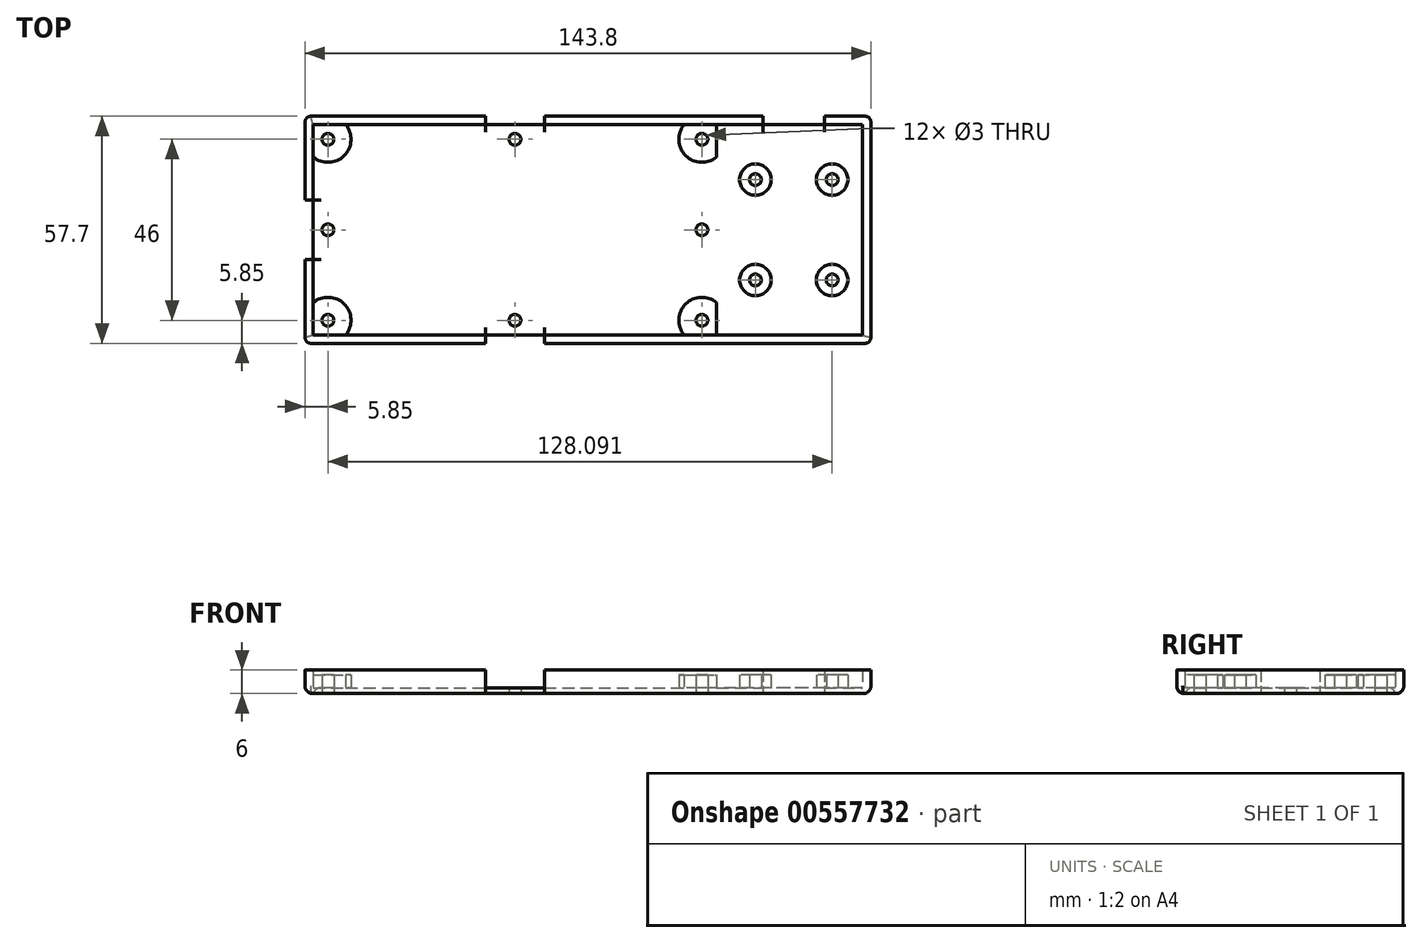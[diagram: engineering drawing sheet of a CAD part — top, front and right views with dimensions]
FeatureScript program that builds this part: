
annotation { "Feature Type Name" : "Feature", "Feature Type Description" : "" }
export const myFeature = defineFeature(function(context is Context, id is Id, definition is map)
    precondition{}
    {
        {
            assignVariable(context, id + "F0", {"name" : "Grosor", "anyValue" : 1.3});
        }
        {
            assignVariable(context, id + "F1", {"name" : "Paredes", "anyValue" : 2.1});
        }
        {
            var Q0;
            Q0=qCreatedBy(makeId("Top.planeOp"),FACE);
            var sketch = newSketch(context, id + "F2", { "sketchPlane" : qUnion([Q0])});
            skLineSegment(sketch, "E0.bottom", {"start": v(-51.25, 26.75) * mm, "end": v(51.25, 26.75) * mm});
            skLineSegment(sketch, "E0.top", {"start": v(-43.01, -26.75) * mm, "end": v(51.25, -26.75) * mm});
            skLineSegment(sketch, "E0.left", {"start": v(-51.25, 26.75) * mm, "end": v(-51.25, -18.51) * mm});
            skLineSegment(sketch, "E0.right", {"start": v(51.25, 26.75) * mm, "end": v(51.25, -26.75) * mm});
            skPoint(sketch, "E0.middle", {"position": v(0, 0) * mm});
            skLineSegment(sketch, "E1.0", {"start": v(-53.35, -28.85) * mm, "end": v(53.35, -28.85) * mm});
            skLineSegment(sketch, "E1.1", {"start": v(-53.35, 28.85) * mm, "end": v(-53.35, -28.85) * mm});
            skLineSegment(sketch, "E1.2", {"start": v(-53.35, 28.85) * mm, "end": v(53.35, 28.85) * mm});
            skLineSegment(sketch, "E1.3", {"start": v(53.35, 28.85) * mm, "end": v(53.35, -28.85) * mm});
            skLineSegment(sketch, "E2.bottom", {"start": v(-47.5, 23) * mm, "end": v(47.5, 23) * mm, "construction": true});
            skLineSegment(sketch, "E2.top", {"start": v(-47.5, -23) * mm, "end": v(47.5, -23) * mm, "construction": true});
            skLineSegment(sketch, "E2.left", {"start": v(-47.5, 23) * mm, "end": v(-47.5, -23) * mm, "construction": true});
            skLineSegment(sketch, "E2.right", {"start": v(47.5, 23) * mm, "end": v(47.5, -23) * mm, "construction": true});
            skCircle(sketch, "E3", {"center": v(47.5, 23) * mm, "radius": 1.5 * mm});
            skCircle(sketch, "E4", {"center": v(47.5, -23) * mm, "radius": 1.5 * mm});
            skCircle(sketch, "E5", {"center": v(-47.5, -23) * mm, "radius": 1.5 * mm});
            skCircle(sketch, "E6", {"center": v(-47.5, 23) * mm, "radius": 1.5 * mm});
            skArc(sketch, "E7", {"start": v(-51.25, 18.51) * mm, "mid": v(-43.36, 18.86) * mm, "end": v(-43.01, 26.75) * mm});
            skArc(sketch, "E8", {"start": v(43.01, 26.75) * mm, "mid": v(43.36, 18.86) * mm, "end": v(51.25, 18.51) * mm});
            skArc(sketch, "E9", {"start": v(51.25, -18.51) * mm, "mid": v(43.36, -18.86) * mm, "end": v(43.01, -26.75) * mm});
            skArc(sketch, "E10.trimOffspring", {"start": v(-43.01, -26.75) * mm, "mid": v(-43.36, -18.86) * mm, "end": v(-51.25, -18.51) * mm});
            skPoint(sketch, "E11.orphan", {"position": v(-51.25, -26.75) * mm});
            skLineSegment(sketch, "E12", {"start": v(-51.25, -18.51) * mm, "end": v(-51.25, -26.75) * mm});
            skLineSegment(sketch, "E13", {"start": v(-43.01, -26.75) * mm, "end": v(-51.25, -26.75) * mm});
            skLineSegment(sketch, "E14.bottom", {"start": v(53.35, -7.5) * mm, "end": v(-53.35, -7.5) * mm});
            skLineSegment(sketch, "E14.top", {"start": v(53.35, 7.5) * mm, "end": v(-53.35, 7.5) * mm});
            skLineSegment(sketch, "E14.left", {"start": v(53.35, -7.5) * mm, "end": v(53.35, 7.5) * mm});
            skLineSegment(sketch, "E14.right", {"start": v(-53.35, -7.5) * mm, "end": v(-53.35, 7.5) * mm});
            skLineSegment(sketch, "E15.bottom", {"start": v(-7.5, 28.85) * mm, "end": v(7.5, 28.85) * mm});
            skLineSegment(sketch, "E15.top", {"start": v(-7.5, -28.85) * mm, "end": v(7.5, -28.85) * mm});
            skLineSegment(sketch, "E15.left", {"start": v(-7.5, 28.85) * mm, "end": v(-7.5, -28.85) * mm});
            skLineSegment(sketch, "E15.right", {"start": v(7.5, 28.85) * mm, "end": v(7.5, -28.85) * mm});
            skCircle(sketch, "E16", {"center": v(-47.5, 0) * mm, "radius": 1.5 * mm});
            skCircle(sketch, "E17", {"center": v(0, 23) * mm, "radius": 1.5 * mm});
            skCircle(sketch, "E18", {"center": v(0, -23) * mm, "radius": 1.5 * mm});
            skCircle(sketch, "E19", {"center": v(47.5, 0) * mm, "radius": 1.5 * mm});
            skLineSegment(sketch, "E20", {"start": v(53.35, 28.85) * mm, "end": v(90.45, 28.85) * mm});
            skLineSegment(sketch, "E21", {"start": v(90.45, 28.85) * mm, "end": v(90.45, -28.85) * mm});
            skLineSegment(sketch, "E22", {"start": v(90.45, -28.85) * mm, "end": v(53.35, -28.85) * mm});
            skLineSegment(sketch, "E23.0", {"start": v(88.35, -26.75) * mm, "end": v(53.35, -26.75) * mm});
            skLineSegment(sketch, "E23.1", {"start": v(88.35, 26.75) * mm, "end": v(88.35, -26.75) * mm});
            skLineSegment(sketch, "E23.2", {"start": v(53.33, 26.75) * mm, "end": v(88.35, 26.75) * mm});
            skLineSegment(sketch, "E24", {"start": v(70.84, 26.75) * mm, "end": v(70.84, 0) * mm, "construction": true});
            skPoint(sketch, "E24.endSnap0", {"position": v(88.35, 0) * mm});
            skLineSegment(sketch, "E25.bottom", {"start": v(80.6, -12.75) * mm, "end": v(61.1, -12.75) * mm, "construction": true});
            skLineSegment(sketch, "E25.top", {"start": v(80.6, 12.75) * mm, "end": v(61.1, 12.75) * mm, "construction": true});
            skLineSegment(sketch, "E25.left", {"start": v(80.6, -12.75) * mm, "end": v(80.6, 12.75) * mm, "construction": true});
            skLineSegment(sketch, "E25.right", {"start": v(61.1, -12.75) * mm, "end": v(61.1, 12.75) * mm, "construction": true});
            skPoint(sketch, "E25.middle", {"position": v(70.84, 0) * mm});
            skCircle(sketch, "E26", {"center": v(61.1, 12.75) * mm, "radius": 1.5 * mm});
            skCircle(sketch, "E27", {"center": v(80.6, 12.75) * mm, "radius": 1.5 * mm});
            skCircle(sketch, "E28", {"center": v(80.6, -12.75) * mm, "radius": 1.5 * mm});
            skCircle(sketch, "E29", {"center": v(61.1, -12.75) * mm, "radius": 1.5 * mm});
            skCircle(sketch, "E30", {"center": v(61.1, 12.75) * mm, "radius": 4 * mm});
            skCircle(sketch, "E31", {"center": v(80.6, 12.75) * mm, "radius": 4 * mm});
            skCircle(sketch, "E32", {"center": v(80.6, -12.75) * mm, "radius": 4 * mm});
            skCircle(sketch, "E33", {"center": v(61.1, -12.75) * mm, "radius": 4 * mm});
            skLineSegment(sketch, "E34", {"start": v(51.25, 26.75) * mm, "end": v(51.25, 28.85) * mm});
            skLineSegment(sketch, "E35", {"start": v(51.25, -26.75) * mm, "end": v(51.25, -28.85) * mm});
            skLineSegment(sketch, "E36", {"start": v(51.25, 26.75) * mm, "end": v(53.33, 26.75) * mm});
            skLineSegment(sketch, "E37", {"start": v(51.25, -26.75) * mm, "end": v(53.35, -26.75) * mm});
            skLineSegment(sketch, "E38.bottom", {"start": v(63, 26.75) * mm, "end": v(78.7, 26.75) * mm});
            skLineSegment(sketch, "E38.top", {"start": v(63, 28.85) * mm, "end": v(78.7, 28.85) * mm});
            skLineSegment(sketch, "E38.left", {"start": v(63, 26.75) * mm, "end": v(63, 28.85) * mm});
            skLineSegment(sketch, "E38.right", {"start": v(78.7, 26.75) * mm, "end": v(78.7, 28.85) * mm});
            skPoint(sketch, "E38.middle", {"position": v(70.84, 27.8) * mm});
            skPoint(sketch, "E38.middle.positionSnap0", {"position": v(51.25, 27.8) * mm});
            skPoint(sketch, "E38.centerSnap0", {"position": v(51.25, 27.8) * mm});
            skSolve(sketch);
        }
        {
            var Q0;
            {var subQ5=sQuery(id+"F2.wireOp",EDGE,"E7");Q0=makeQuery(id+"F2.imprint","IMPRINT",FACE,{"disambiguationData":[TD([[makeQuery(id+"F2.imprint","IMPRINT",EDGE,{"derivedFrom":subQ5}),-1.0]])]});}
            var Q1;
            Q1=makeQuery(id+"F2.imprint","IMPRINT",FACE,{"disambiguationData":[TD([[makeQuery(id+"F2.imprint","IMPRINT",EDGE,{"derivedFrom":sQuery(id+"F2.wireOp",EDGE,"E16")}),-1.0]])]});
            var Q2;
            {var subQ7=sQuery(id+"F2.wireOp",EDGE,"E10.trimOffspring");Q2=makeQuery(id+"F2.imprint","IMPRINT",FACE,{"disambiguationData":[TD([[makeQuery(id+"F2.imprint","IMPRINT",EDGE,{"derivedFrom":subQ7}),-1.0]])]});}
            var Q3;
            Q3=makeQuery(id+"F2.imprint","IMPRINT",FACE,{"disambiguationData":[TD([[makeQuery(id+"F2.imprint","IMPRINT",EDGE,{"derivedFrom":sQuery(id+"F2.wireOp",EDGE,"E18")}),-1.0]])]});
            var Q4;
            {var subQ5=sQuery(id+"F2.wireOp",EDGE,"E9");Q4=makeQuery(id+"F2.imprint","IMPRINT",FACE,{"disambiguationData":[TD([[makeQuery(id+"F2.imprint","IMPRINT",EDGE,{"derivedFrom":subQ5}),-1.0]])]});}
            var Q5;
            Q5=makeQuery(id+"F2.imprint","IMPRINT",FACE,{"disambiguationData":[TD([[makeQuery(id+"F2.imprint","IMPRINT",EDGE,{"derivedFrom":sQuery(id+"F2.wireOp",EDGE,"E19")}),-1.0]])]});
            var Q6;
            {var subQ7=sQuery(id+"F2.wireOp",EDGE,"E8");Q6=makeQuery(id+"F2.imprint","IMPRINT",FACE,{"disambiguationData":[TD([[makeQuery(id+"F2.imprint","IMPRINT",EDGE,{"derivedFrom":subQ7}),-1.0]])]});}
            var Q7;
            Q7=makeQuery(id+"F2.imprint","IMPRINT",FACE,{"disambiguationData":[TD([[makeQuery(id+"F2.imprint","IMPRINT",EDGE,{"derivedFrom":sQuery(id+"F2.wireOp",EDGE,"E17")}),-1.0]])]});
            var Q8;
            {var subQ0=sQuery(id+"F2.wireOp",EDGE,"E15.left");var subQ1=sQuery(id+"F2.wireOp",EDGE,"E14.bottom");var subQ2=makeQuery(id+"F2.imprint","INTERSECT",VERTEX,{"derivedFrom":[subQ1,subQ0]});Q8=makeQuery(id+"F2.imprint","IMPRINT",FACE,{"disambiguationData":[TD([[makeQuery(id+"F2.imprint","IMPRINT",EDGE,{"disambiguationData":[TD([[subQ2,1.0]])],"derivedFrom":subQ1}),-1.0]])]});}
            var Q9;
            {var subQ8=sQuery(id+"F2.wireOp",EDGE,"E23.0");Q9=makeQuery(id+"F2.imprint","IMPRINT",FACE,{"disambiguationData":[TD([[makeQuery(id+"F2.imprint","IMPRINT",EDGE,{"derivedFrom":subQ8}),-1.0]])]});}
            var Q10;
            {var subQ8=sQuery(id+"F2.wireOp",EDGE,"E36");Q10=makeQuery(id+"F2.imprint","IMPRINT",FACE,{"disambiguationData":[TD([[makeQuery(id+"F2.imprint","IMPRINT",EDGE,{"derivedFrom":subQ8}),-1.0]])]});}
            var Q11;
            {var subQ0=sQuery(id+"F2.wireOp",EDGE,"E14.top");var subQ1=sQuery(id+"F2.wireOp",EDGE,"E0.right");var subQ2=makeQuery(id+"F2.imprint","INTERSECT",VERTEX,{"derivedFrom":[subQ1,subQ0]});Q11=makeQuery(id+"F2.imprint","IMPRINT",FACE,{"disambiguationData":[TD([[makeQuery(id+"F2.imprint","IMPRINT",EDGE,{"disambiguationData":[TD([[subQ2,-1.0]])],"derivedFrom":subQ1}),1.0]])]});}
            var Q12;
            {var subQ5=sQuery(id+"F2.wireOp",EDGE,"E37");Q12=makeQuery(id+"F2.imprint","IMPRINT",FACE,{"disambiguationData":[TD([[makeQuery(id+"F2.imprint","IMPRINT",EDGE,{"derivedFrom":subQ5}),1.0]])]});}
            extrude(context, id + "F3", {"entities" : qUnion([Q0, Q1, Q2, Q3, Q4, Q5, Q6, Q7, Q8, Q9, Q10, Q11, Q12]), "depth" : (getVariable(context, 'Paredes') - 0.6) * mm, "offsetDistance" : 25 * mm});
        }
        {
            var Q0;
            Q0=makeQuery(id+"F2.imprint","IMPRINT",FACE,{"disambiguationData":[TD([[makeQuery(id+"F2.imprint","IMPRINT",EDGE,{"derivedFrom":sQuery(id+"F2.wireOp",EDGE,"E5")}),-1.0]])]});
            var Q1;
            Q1=makeQuery(id+"F2.imprint","IMPRINT",FACE,{"disambiguationData":[TD([[makeQuery(id+"F2.imprint","IMPRINT",EDGE,{"derivedFrom":sQuery(id+"F2.wireOp",EDGE,"E4")}),-1.0]])]});
            var Q2;
            Q2=makeQuery(id+"F2.imprint","IMPRINT",FACE,{"disambiguationData":[TD([[makeQuery(id+"F2.imprint","IMPRINT",EDGE,{"derivedFrom":sQuery(id+"F2.wireOp",EDGE,"E3")}),-1.0]])]});
            var Q3;
            Q3=makeQuery(id+"F2.imprint","IMPRINT",FACE,{"disambiguationData":[TD([[makeQuery(id+"F2.imprint","IMPRINT",EDGE,{"derivedFrom":sQuery(id+"F2.wireOp",EDGE,"E6")}),-1.0]])]});
            var Q4;
            Q4=makeQuery(id+"F2.imprint","IMPRINT",FACE,{"disambiguationData":[TD([[makeQuery(id+"F2.imprint","IMPRINT",EDGE,{"derivedFrom":sQuery(id+"F2.wireOp",EDGE,"E26")}),-1.0]])]});
            var Q5;
            Q5=makeQuery(id+"F2.imprint","IMPRINT",FACE,{"disambiguationData":[TD([[makeQuery(id+"F2.imprint","IMPRINT",EDGE,{"derivedFrom":sQuery(id+"F2.wireOp",EDGE,"E27")}),-1.0]])]});
            var Q6;
            Q6=makeQuery(id+"F2.imprint","IMPRINT",FACE,{"disambiguationData":[TD([[makeQuery(id+"F2.imprint","IMPRINT",EDGE,{"derivedFrom":sQuery(id+"F2.wireOp",EDGE,"E29")}),-1.0]])]});
            var Q7;
            Q7=makeQuery(id+"F2.imprint","IMPRINT",FACE,{"disambiguationData":[TD([[makeQuery(id+"F2.imprint","IMPRINT",EDGE,{"derivedFrom":sQuery(id+"F2.wireOp",EDGE,"E28")}),-1.0]])]});
            extrude(context, id + "F4", {"entities" : qUnion([Q0, Q1, Q2, Q3, Q4, Q5, Q6, Q7]), "operationType" : NewBodyOperationType.ADD, "depth" : (getVariable(context, 'Paredes') + (getVariable(context, 'Grosor') * 2)) * mm, "offsetDistance" : 25 * mm});
        }
        {
            var Q0;
            {var subQ7=sQuery(id+"F2.wireOp",EDGE,"E12");Q0=makeQuery(id+"F2.imprint","IMPRINT",FACE,{"disambiguationData":[TD([[makeQuery(id+"F2.imprint","IMPRINT",EDGE,{"derivedFrom":subQ7}),-1.0]])]});}
            var Q1;
            {var subQ3=sQuery(id+"F2.wireOp",EDGE,"E35");Q1=makeQuery(id+"F2.imprint","IMPRINT",FACE,{"disambiguationData":[TD([[makeQuery(id+"F2.imprint","IMPRINT",EDGE,{"derivedFrom":subQ3}),-1.0]])]});}
            var Q2;
            {var subQ0=sQuery(id+"F2.wireOp",EDGE,"E7");var subQ3=sQuery(id+"F2.wireOp",EDGE,"E0.bottom");var subQ5=makeQuery(id+"F2.imprint","INTERSECT",VERTEX,{"derivedFrom":[subQ3,subQ0]});Q2=makeQuery(id+"F2.imprint","IMPRINT",FACE,{"disambiguationData":[TD([[makeQuery(id+"F2.imprint","IMPRINT",EDGE,{"disambiguationData":[TD([[subQ5,-1.0]])],"derivedFrom":subQ3}),1.0]])]});}
            var Q3;
            {var subQ5=sQuery(id+"F2.wireOp",EDGE,"E34");Q3=makeQuery(id+"F2.imprint","IMPRINT",FACE,{"disambiguationData":[TD([[makeQuery(id+"F2.imprint","IMPRINT",EDGE,{"derivedFrom":subQ5}),1.0]])]});}
            var Q4;
            {var subQ5=sQuery(id+"F2.wireOp",EDGE,"E38.left");Q4=makeQuery(id+"F2.imprint","IMPRINT",FACE,{"disambiguationData":[TD([[makeQuery(id+"F2.imprint","IMPRINT",EDGE,{"derivedFrom":subQ5}),1.0]])]});}
            var Q5;
            {var subQ0=sQuery(id+"F2.wireOp",EDGE,"E34");Q5=makeQuery(id+"F2.imprint","IMPRINT",FACE,{"disambiguationData":[TD([[makeQuery(id+"F2.imprint","IMPRINT",EDGE,{"derivedFrom":subQ0}),-1.0]])]});}
            var Q6;
            {var subQ3=sQuery(id+"F2.wireOp",EDGE,"E35");Q6=makeQuery(id+"F2.imprint","IMPRINT",FACE,{"disambiguationData":[TD([[makeQuery(id+"F2.imprint","IMPRINT",EDGE,{"derivedFrom":subQ3}),1.0]])]});}
            var Q7;
            {var subQ1=sQuery(id+"F2.wireOp",EDGE,"E21");Q7=makeQuery(id+"F2.imprint","IMPRINT",FACE,{"disambiguationData":[TD([[makeQuery(id+"F2.imprint","IMPRINT",EDGE,{"derivedFrom":subQ1}),-1.0]])]});}
            extrude(context, id + "F5", {"entities" : qUnion([Q0, Q1, Q2, Q3, Q4, Q5, Q6, Q7]), "operationType" : NewBodyOperationType.ADD, "depth" : (getVariable(context, 'Paredes') + (getVariable(context, 'Grosor') * 3)) * mm, "offsetDistance" : 25 * mm});
        }
        {
            var Q0;
            Q0=makeQuery(id+"F5.opExtrude","SWEPT_EDGE",EDGE,{"disambiguationData":[OSD([sQuery(id+"F2.wireOp",EDGE,"E1.0"),sQuery(id+"F2.wireOp",EDGE,"E1.1")])]});
            var Q1;
            Q1=makeQuery(id+"F5.opExtrude","SWEPT_EDGE",EDGE,{"disambiguationData":[OSD([sQuery(id+"F2.wireOp",EDGE,"E1.1"),sQuery(id+"F2.wireOp",EDGE,"E1.2")])]});
            var Q2;
            Q2=makeQuery(id+"F5.opExtrude","SWEPT_EDGE",EDGE,{"disambiguationData":[OSD([sQuery(id+"F2.wireOp",EDGE,"E1.1"),sQuery(id+"F2.wireOp",EDGE,"E1.2")])]});
            var Q3;
            Q3=makeQuery(id+"F5.opExtrude","SWEPT_EDGE",EDGE,{"disambiguationData":[OSD([sQuery(id+"F2.wireOp",EDGE,"E1.0"),sQuery(id+"F2.wireOp",EDGE,"E1.1")])]});
            var Q4;
            Q4=makeQuery(id+"F5.opExtrude","SWEPT_EDGE",EDGE,{"disambiguationData":[OSD([sQuery(id+"F2.wireOp",EDGE,"E21"),sQuery(id+"F2.wireOp",EDGE,"E22")])]});
            var Q5;
            Q5=makeQuery(id+"F5.opExtrude","SWEPT_EDGE",EDGE,{"disambiguationData":[OSD([sQuery(id+"F2.wireOp",EDGE,"E20"),sQuery(id+"F2.wireOp",EDGE,"E21")])]});
            fillet(context, id + "F6", {"entities" : qUnion([Q0, Q1, Q2, Q3, Q4, Q5]), "radius" : 1.5 * mm, "tangentPropagation" : true, "allowEdgeOverflow" : false});
        }
        {
            var Q0;
            {var subQ0=sQuery(id+"F2.wireOp",EDGE,"E0.bottom");Q0=makeQuery(id+"F5.boolean.opBoolean","SPLIT",EDGE,{"disambiguationData":[topologyDisambiguationEdgeConnected([makeQuery(id+"F5.opExtrude","SWEPT_FACE",FACE,{"disambiguationData":[OSD([subQ0])]})])],"derivedFrom":makeQuery(id+"F3.opExtrude","CAP_EDGE",EDGE,{"disambiguationData":[OSD([subQ0])],"isStart":false})});}
            var Q1;
            Q1=makeQuery(id+"F3.opExtrude","CAP_EDGE",EDGE,{"disambiguationData":[OSD([sQuery(id+"F2.wireOp",EDGE,"E7")])],"isStart":false});
            var Q2;
            {var subQ0=sQuery(id+"F2.wireOp",EDGE,"E36");var subQ1=sQuery(id+"F2.wireOp",EDGE,"E23.2");var subQ2=sQuery(id+"F2.wireOp",EDGE,"E0.bottom");Q2=makeQuery(id+"F5.boolean.opBoolean","SPLIT",EDGE,{"disambiguationData":[topologyDisambiguationEdgeConnected([makeQuery(id+"F5.opExtrude","SWEPT_FACE",FACE,{"disambiguationData":[OSD([subQ2,subQ1,subQ0])]})])],"derivedFrom":makeQuery(id+"F3.opExtrude","CAP_EDGE",EDGE,{"disambiguationData":[OSD([subQ2])],"isStart":false})});}
            var Q3;
            {var subQ0=sQuery(id+"F2.wireOp",EDGE,"E36");var subQ1=sQuery(id+"F2.wireOp",EDGE,"E23.2");var subQ2=sQuery(id+"F2.wireOp",EDGE,"E0.bottom");Q3=makeQuery(id+"F5.boolean.opBoolean","SPLIT",EDGE,{"disambiguationData":[topologyDisambiguationEdgeConnected([makeQuery(id+"F5.opExtrude","SWEPT_FACE",FACE,{"disambiguationData":[OSD([subQ2,subQ1,subQ0])]})])],"derivedFrom":makeQuery(id+"F3.opExtrude","CAP_EDGE",EDGE,{"disambiguationData":[OSD([subQ1,subQ0])],"isStart":false})});}
            var Q4;
            Q4=makeQuery(id+"F3.opExtrude","CAP_EDGE",EDGE,{"disambiguationData":[OSD([sQuery(id+"F2.wireOp",EDGE,"E8")])],"isStart":false});
            var Q5;
            Q5=makeQuery(id+"F3.opExtrude","CAP_EDGE",EDGE,{"disambiguationData":[OSD([sQuery(id+"F2.wireOp",EDGE,"E30")])],"isStart":false});
            var Q6;
            Q6=makeQuery(id+"F3.opExtrude","CAP_EDGE",EDGE,{"disambiguationData":[OSD([sQuery(id+"F2.wireOp",EDGE,"E31")])],"isStart":false});
            var Q7;
            Q7=makeQuery(id+"F3.opExtrude","CAP_EDGE",EDGE,{"disambiguationData":[OSD([sQuery(id+"F2.wireOp",EDGE,"E33")])],"isStart":false});
            var Q8;
            Q8=makeQuery(id+"F3.opExtrude","CAP_EDGE",EDGE,{"disambiguationData":[OSD([sQuery(id+"F2.wireOp",EDGE,"E32")])],"isStart":false});
            var Q9;
            {var subQ0=sQuery(id+"F2.wireOp",EDGE,"E36");var subQ1=sQuery(id+"F2.wireOp",EDGE,"E23.2");Q9=makeQuery(id+"F5.boolean.opBoolean","SPLIT",EDGE,{"disambiguationData":[topologyDisambiguationEdgeConnected([makeQuery(id+"F5.opExtrude","SWEPT_FACE",FACE,{"disambiguationData":[OSD([subQ1])]})])],"derivedFrom":makeQuery(id+"F3.opExtrude","CAP_EDGE",EDGE,{"disambiguationData":[OSD([subQ1,subQ0])],"isStart":false})});}
            var Q10;
            Q10=makeQuery(id+"F3.opExtrude","CAP_EDGE",EDGE,{"disambiguationData":[OSD([sQuery(id+"F2.wireOp",EDGE,"E23.1")])],"isStart":false});
            var Q11;
            {var subQ0=sQuery(id+"F2.wireOp",EDGE,"E0.left");Q11=makeQuery(id+"F5.boolean.opBoolean","SPLIT",EDGE,{"disambiguationData":[topologyDisambiguationEdgeConnected([makeQuery(id+"F5.opExtrude","SWEPT_FACE",FACE,{"disambiguationData":[OSD([subQ0])]})])],"derivedFrom":makeQuery(id+"F3.opExtrude","CAP_EDGE",EDGE,{"disambiguationData":[OSD([subQ0])],"isStart":false})});}
            var Q12;
            {var subQ0=sQuery(id+"F2.wireOp",EDGE,"E0.left");Q12=makeQuery(id+"F5.boolean.opBoolean","SPLIT",EDGE,{"disambiguationData":[topologyDisambiguationEdgeConnected([makeQuery(id+"F5.opExtrude","SWEPT_FACE",FACE,{"disambiguationData":[OSD([subQ0,sQuery(id+"F2.wireOp",EDGE,"E12")])]})])],"derivedFrom":makeQuery(id+"F3.opExtrude","CAP_EDGE",EDGE,{"disambiguationData":[OSD([subQ0])],"isStart":false})});}
            var Q13;
            {var subQ0=sQuery(id+"F2.wireOp",EDGE,"E0.top");Q13=makeQuery(id+"F5.boolean.opBoolean","SPLIT",EDGE,{"disambiguationData":[topologyDisambiguationEdgeConnected([makeQuery(id+"F5.opExtrude","SWEPT_FACE",FACE,{"disambiguationData":[OSD([subQ0,sQuery(id+"F2.wireOp",EDGE,"E13")])]})])],"derivedFrom":makeQuery(id+"F3.opExtrude","CAP_EDGE",EDGE,{"disambiguationData":[OSD([subQ0])],"isStart":false})});}
            var Q14;
            Q14=makeQuery(id+"F3.opExtrude","CAP_EDGE",EDGE,{"disambiguationData":[OSD([sQuery(id+"F2.wireOp",EDGE,"E10.trimOffspring")])],"isStart":false});
            var Q15;
            {var subQ0=sQuery(id+"F2.wireOp",EDGE,"E37");var subQ1=sQuery(id+"F2.wireOp",EDGE,"E23.0");var subQ2=sQuery(id+"F2.wireOp",EDGE,"E0.top");Q15=makeQuery(id+"F5.boolean.opBoolean","SPLIT",EDGE,{"disambiguationData":[topologyDisambiguationEdgeConnected([makeQuery(id+"F5.opExtrude","SWEPT_FACE",FACE,{"disambiguationData":[OSD([subQ2,subQ1,subQ0])]})])],"derivedFrom":makeQuery(id+"F3.opExtrude","CAP_EDGE",EDGE,{"disambiguationData":[OSD([subQ2])],"isStart":false})});}
            var Q16;
            Q16=makeQuery(id+"F3.opExtrude","CAP_EDGE",EDGE,{"disambiguationData":[OSD([sQuery(id+"F2.wireOp",EDGE,"E9")])],"isStart":false});
            var Q17;
            {var subQ0=sQuery(id+"F2.wireOp",EDGE,"E0.right");Q17=makeQuery(id+"F3.opExtrude","CAP_EDGE",EDGE,{"disambiguationData":[OSD([subQ0]),TDD([makeQuery(id+"F2.imprint","IMPRINT",EDGE,{"disambiguationData":[TD([[makeQuery(id+"F2.imprint","INTERSECT",VERTEX,{"derivedFrom":[subQ0,sQuery(id+"F2.wireOp",EDGE,"E8")]}),1.0]])],"derivedFrom":subQ0})])],"isStart":false});}
            var Q18;
            {var subQ0=sQuery(id+"F2.wireOp",EDGE,"E0.right");Q18=makeQuery(id+"F3.opExtrude","CAP_EDGE",EDGE,{"disambiguationData":[OSD([subQ0]),TDD([makeQuery(id+"F2.imprint","IMPRINT",EDGE,{"disambiguationData":[TD([[makeQuery(id+"F2.imprint","INTERSECT",VERTEX,{"derivedFrom":[subQ0,sQuery(id+"F2.wireOp",EDGE,"E9")]}),-1.0]])],"derivedFrom":subQ0})])],"isStart":false});}
            var Q19;
            Q19=makeQuery(id+"F3.opExtrude","CAP_EDGE",EDGE,{"disambiguationData":[OSD([sQuery(id+"F2.wireOp",EDGE,"E23.0"),sQuery(id+"F2.wireOp",EDGE,"E37")])],"isStart":false});
            fillet(context, id + "F7", {"entities" : qUnion([Q0, Q1, Q2, Q3, Q4, Q5, Q6, Q7, Q8, Q9, Q10, Q11, Q12, Q13, Q14, Q15, Q16, Q17, Q18, Q19]), "radius" : 2 * mm, "tangentPropagation" : true, "allowEdgeOverflow" : false});
        }
        {
            var Q0;
            Q0=makeQuery(id+"F5.opExtrude","CAP_EDGE",EDGE,{"disambiguationData":[OSD([sQuery(id+"F2.wireOp",EDGE,"E1.0")])],"isStart":true});
            var Q1;
            {var subQ0=sQuery(id+"F2.wireOp",EDGE,"E37");var subQ1=sQuery(id+"F2.wireOp",EDGE,"E23.2");var subQ2=sQuery(id+"F2.wireOp",EDGE,"E23.1");var subQ3=sQuery(id+"F2.wireOp",EDGE,"E23.0");var subQ4=sQuery(id+"F2.wireOp",EDGE,"E20");var subQ5=sQuery(id+"F2.wireOp",EDGE,"E15.right");var subQ6=sQuery(id+"F2.wireOp",EDGE,"E1.0");var subQ7=sQuery(id+"F2.wireOp",EDGE,"E0.top");var subQ8=sQuery(id+"F2.wireOp",EDGE,"E15.left");var subQ9=sQuery(id+"F2.wireOp",EDGE,"E13");var subQ10=sQuery(id+"F2.wireOp",EDGE,"E12");var subQ11=sQuery(id+"F2.wireOp",EDGE,"E1.1");var subQ12=sQuery(id+"F2.wireOp",EDGE,"E0.left");var subQ13=sQuery(id+"F2.wireOp",EDGE,"E1.2");var subQ14=sQuery(id+"F2.wireOp",EDGE,"E0.bottom");var subQ15=sQuery(id+"F2.wireOp",EDGE,"E36");var subQ16=sQuery(id+"F2.wireOp",EDGE,"E33");var subQ17=sQuery(id+"F2.wireOp",EDGE,"E32");var subQ18=sQuery(id+"F2.wireOp",EDGE,"E31");var subQ19=sQuery(id+"F2.wireOp",EDGE,"E30");var subQ20=sQuery(id+"F2.wireOp",EDGE,"E10.trimOffspring");var subQ21=sQuery(id+"F2.wireOp",EDGE,"E9");var subQ22=sQuery(id+"F2.wireOp",EDGE,"E0.right");var subQ23=sQuery(id+"F2.wireOp",EDGE,"E7");var subQ24=sQuery(id+"F2.wireOp",EDGE,"E8");Q1=makeQuery(id+"F6.opFillet","BLEND_EDGE",EDGE,{"blendedFrom":[makeQuery(id+"F5.opExtrude","SWEPT_EDGE",EDGE,{"disambiguationData":[OSD([subQ6,subQ11])]}),makeQuery(id+"F5.boolean.opBoolean","MERGE",FACE,{"derivedFrom":[makeQuery(id+"F4.boolean.opBoolean","MERGE",FACE,{"derivedFrom":[makeQuery(id+"F3.opExtrude","CAP_FACE",FACE,{"disambiguationData":[OSD([subQ14,subQ7,subQ12,subQ22,subQ23,subQ24,subQ21,subQ20,sQuery(id+"F2.wireOp",EDGE,"E16"),sQuery(id+"F2.wireOp",EDGE,"E17"),sQuery(id+"F2.wireOp",EDGE,"E18"),sQuery(id+"F2.wireOp",EDGE,"E19"),subQ3,subQ2,subQ1,subQ19,subQ18,subQ17,subQ16,subQ15,subQ0])],"isStart":true}),makeQuery(id+"F4.opExtrude","CAP_FACE",FACE,{"disambiguationData":[OSD([subQ14,subQ22,sQuery(id+"F2.wireOp",EDGE,"E3"),subQ24])],"isStart":true}),makeQuery(id+"F4.opExtrude","CAP_FACE",FACE,{"disambiguationData":[OSD([subQ14,subQ12,sQuery(id+"F2.wireOp",EDGE,"E6"),subQ23])],"isStart":true}),makeQuery(id+"F4.opExtrude","CAP_FACE",FACE,{"disambiguationData":[OSD([subQ7,subQ22,sQuery(id+"F2.wireOp",EDGE,"E4"),subQ21])],"isStart":true}),makeQuery(id+"F4.opExtrude","CAP_FACE",FACE,{"disambiguationData":[OSD([sQuery(id+"F2.wireOp",EDGE,"E5"),subQ20,subQ10,subQ9])],"isStart":true}),makeQuery(id+"F4.opExtrude","CAP_FACE",FACE,{"disambiguationData":[OSD([sQuery(id+"F2.wireOp",EDGE,"E26"),subQ19])],"isStart":true}),makeQuery(id+"F4.opExtrude","CAP_FACE",FACE,{"disambiguationData":[OSD([sQuery(id+"F2.wireOp",EDGE,"E27"),subQ18])],"isStart":true}),makeQuery(id+"F4.opExtrude","CAP_FACE",FACE,{"disambiguationData":[OSD([sQuery(id+"F2.wireOp",EDGE,"E28"),subQ17])],"isStart":true}),makeQuery(id+"F4.opExtrude","CAP_FACE",FACE,{"disambiguationData":[OSD([sQuery(id+"F2.wireOp",EDGE,"E29"),subQ16])],"isStart":true})]}),makeQuery(id+"F5.opExtrude","CAP_FACE",FACE,{"disambiguationData":[OSD([subQ14,subQ13,subQ5,subQ4,subQ1,subQ15,sQuery(id+"F2.wireOp",EDGE,"E38.left")])],"isStart":true}),makeQuery(id+"F5.opExtrude","CAP_FACE",FACE,{"disambiguationData":[OSD([subQ14,subQ12,subQ11,subQ13,sQuery(id+"F2.wireOp",EDGE,"E14.top"),subQ8])],"isStart":true}),makeQuery(id+"F5.opExtrude","CAP_FACE",FACE,{"disambiguationData":[OSD([subQ7,subQ12,subQ6,subQ11,subQ10,subQ9,sQuery(id+"F2.wireOp",EDGE,"E14.bottom"),subQ8])],"isStart":true}),makeQuery(id+"F5.opExtrude","CAP_FACE",FACE,{"disambiguationData":[OSD([subQ7,subQ6,subQ5,subQ4,sQuery(id+"F2.wireOp",EDGE,"E21"),sQuery(id+"F2.wireOp",EDGE,"E22"),subQ3,subQ2,subQ1,subQ0,sQuery(id+"F2.wireOp",EDGE,"E38.right")])],"isStart":true})]})],"blendedInto":[makeQuery(id+"F5.boolean.opBoolean","MERGE",FACE,{"derivedFrom":[makeQuery(id+"F4.boolean.opBoolean","MERGE",FACE,{"derivedFrom":[makeQuery(id+"F3.opExtrude","CAP_FACE",FACE,{"disambiguationData":[OSD([subQ14,subQ7,subQ12,subQ22,subQ23,subQ24,subQ21,subQ20,sQuery(id+"F2.wireOp",EDGE,"E16"),sQuery(id+"F2.wireOp",EDGE,"E17"),sQuery(id+"F2.wireOp",EDGE,"E18"),sQuery(id+"F2.wireOp",EDGE,"E19"),subQ3,subQ2,subQ1,subQ19,subQ18,subQ17,subQ16,subQ15,subQ0])],"isStart":true}),makeQuery(id+"F4.opExtrude","CAP_FACE",FACE,{"disambiguationData":[OSD([subQ14,subQ22,sQuery(id+"F2.wireOp",EDGE,"E3"),subQ24])],"isStart":true}),makeQuery(id+"F4.opExtrude","CAP_FACE",FACE,{"disambiguationData":[OSD([subQ14,subQ12,sQuery(id+"F2.wireOp",EDGE,"E6"),subQ23])],"isStart":true}),makeQuery(id+"F4.opExtrude","CAP_FACE",FACE,{"disambiguationData":[OSD([subQ7,subQ22,sQuery(id+"F2.wireOp",EDGE,"E4"),subQ21])],"isStart":true}),makeQuery(id+"F4.opExtrude","CAP_FACE",FACE,{"disambiguationData":[OSD([sQuery(id+"F2.wireOp",EDGE,"E5"),subQ20,subQ10,subQ9])],"isStart":true}),makeQuery(id+"F4.opExtrude","CAP_FACE",FACE,{"disambiguationData":[OSD([sQuery(id+"F2.wireOp",EDGE,"E26"),subQ19])],"isStart":true}),makeQuery(id+"F4.opExtrude","CAP_FACE",FACE,{"disambiguationData":[OSD([sQuery(id+"F2.wireOp",EDGE,"E27"),subQ18])],"isStart":true}),makeQuery(id+"F4.opExtrude","CAP_FACE",FACE,{"disambiguationData":[OSD([sQuery(id+"F2.wireOp",EDGE,"E28"),subQ17])],"isStart":true}),makeQuery(id+"F4.opExtrude","CAP_FACE",FACE,{"disambiguationData":[OSD([sQuery(id+"F2.wireOp",EDGE,"E29"),subQ16])],"isStart":true})]}),makeQuery(id+"F5.opExtrude","CAP_FACE",FACE,{"disambiguationData":[OSD([subQ14,subQ13,subQ5,subQ4,subQ1,subQ15,sQuery(id+"F2.wireOp",EDGE,"E38.left")])],"isStart":true}),makeQuery(id+"F5.opExtrude","CAP_FACE",FACE,{"disambiguationData":[OSD([subQ14,subQ12,subQ11,subQ13,sQuery(id+"F2.wireOp",EDGE,"E14.top"),subQ8])],"isStart":true}),makeQuery(id+"F5.opExtrude","CAP_FACE",FACE,{"disambiguationData":[OSD([subQ7,subQ12,subQ6,subQ11,subQ10,subQ9,sQuery(id+"F2.wireOp",EDGE,"E14.bottom"),subQ8])],"isStart":true}),makeQuery(id+"F5.opExtrude","CAP_FACE",FACE,{"disambiguationData":[OSD([subQ7,subQ6,subQ5,subQ4,sQuery(id+"F2.wireOp",EDGE,"E21"),sQuery(id+"F2.wireOp",EDGE,"E22"),subQ3,subQ2,subQ1,subQ0,sQuery(id+"F2.wireOp",EDGE,"E38.right")])],"isStart":true})]})]});}
            var Q2;
            {var subQ0=sQuery(id+"F2.wireOp",EDGE,"E1.1");Q2=makeQuery(id+"F5.opExtrude","CAP_EDGE",EDGE,{"disambiguationData":[OSD([subQ0]),TDD([makeQuery(id+"F2.imprint","IMPRINT",EDGE,{"disambiguationData":[TD([[makeQuery(id+"F2.imprint","INTERSECT",VERTEX,{"derivedFrom":[sQuery(id+"F2.wireOp",EDGE,"E1.0"),subQ0]}),1.0]])],"derivedFrom":subQ0})])],"isStart":true});}
            var Q3;
            Q3=makeQuery(id+"F5.opExtrude","CAP_EDGE",EDGE,{"disambiguationData":[OSD([sQuery(id+"F2.wireOp",EDGE,"E1.0"),sQuery(id+"F2.wireOp",EDGE,"E22")])],"isStart":true});
            var Q4;
            Q4=makeQuery(id+"F5.opExtrude","CAP_EDGE",EDGE,{"disambiguationData":[OSD([sQuery(id+"F2.wireOp",EDGE,"E1.2"),sQuery(id+"F2.wireOp",EDGE,"E20")])],"isStart":true});
            var Q5;
            Q5=makeQuery(id+"F5.opExtrude","CAP_EDGE",EDGE,{"disambiguationData":[OSD([sQuery(id+"F2.wireOp",EDGE,"E1.2")])],"isStart":true});
            fillet(context, id + "F8", {"entities" : qUnion([Q0, Q1, Q2, Q3, Q4, Q5]), "radius" : 2 * mm, "tangentPropagation" : true, "allowEdgeOverflow" : false});
        }
    });
